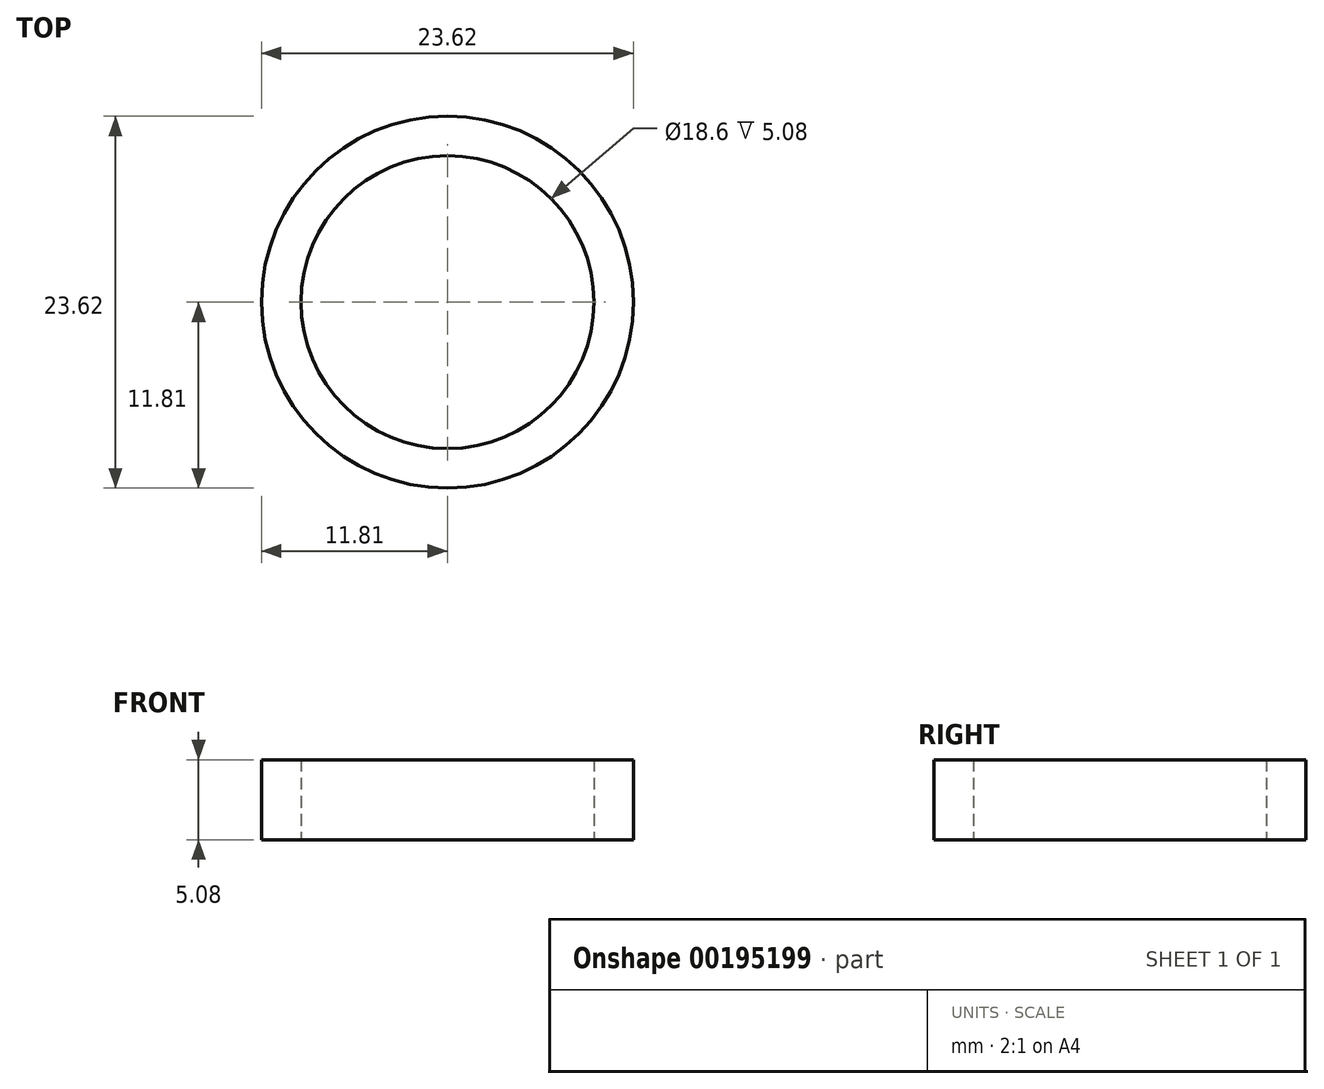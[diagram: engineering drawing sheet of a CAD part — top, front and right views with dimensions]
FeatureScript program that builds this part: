
annotation { "Feature Type Name" : "Feature", "Feature Type Description" : "" }
export const myFeature = defineFeature(function(context is Context, id is Id, definition is map)
    precondition{}
    {
        {
            var Q0;
            Q0=qCreatedBy(makeId("Top.planeOp"),FACE);
            var sketch = newSketch(context, id + "F0", { "sketchPlane" : qUnion([Q0])});
            skCircle(sketch, "E0", {"center": v(0, 0) * mm, "radius": 9.3 * mm});
            skCircle(sketch, "E1", {"center": v(0, 0) * mm, "radius": 11.81 * mm});
            skSolve(sketch);
        }
        {
            var Q0;
            Q0 = qSketchRegion(id + "F0", true);
            extrude(context, id + "F1", {"entities" : qUnion([Q0]), "depth" : 5.08 * mm});
        }
    });
